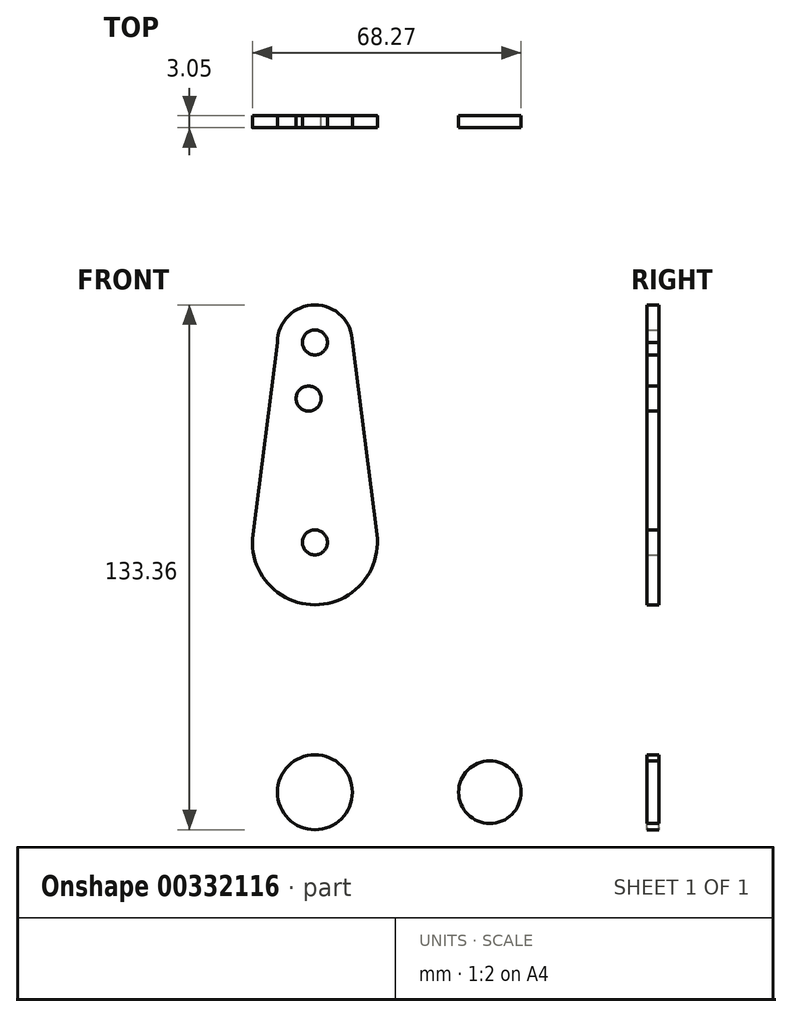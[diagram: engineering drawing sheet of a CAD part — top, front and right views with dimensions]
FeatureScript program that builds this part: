
annotation { "Feature Type Name" : "Feature", "Feature Type Description" : "" }
export const myFeature = defineFeature(function(context is Context, id is Id, definition is map)
    precondition{}
    {
        {
            var Q0;
            Q0=qCreatedBy(makeId("Front.planeOp"),FACE);
            var sketch = newSketch(context, id + "F0", { "sketchPlane" : qUnion([Q0])});
            skLineSegment(sketch, "E0", {"start": v(0, 0) * mm, "end": v(0, 114.3) * mm, "construction": true});
            skLineSegment(sketch, "E1", {"start": v(0, 0) * mm, "end": v(44.45, 0) * mm, "construction": true});
            skCircle(sketch, "E2", {"center": v(0, 114.3) * mm, "radius": 9.53 * mm});
            skCircle(sketch, "E3", {"center": v(0, 63.5) * mm, "radius": 15.88 * mm});
            skCircle(sketch, "E4", {"center": v(0, 0) * mm, "radius": 9.53 * mm});
            skCircle(sketch, "E5", {"center": v(44.45, 0) * mm, "radius": 7.94 * mm});
            skLineSegment(sketch, "E6", {"start": v(-9.53, 114.3) * mm, "end": v(-15.75, 65.5) * mm});
            skLineSegment(sketch, "E7", {"start": v(9.53, 114.3) * mm, "end": v(15.75, 65.5) * mm});
            skLineSegment(sketch, "E8", {"start": v(18.97, 8.85) * mm, "end": v(44.73, 7.93) * mm});
            skLineSegment(sketch, "E9", {"start": v(0, -9.52) * mm, "end": v(44.45, -7.94) * mm});
            skLineSegment(sketch, "E10", {"start": v(15.8, 61.91) * mm, "end": v(11.34, 17.59) * mm});
            skLineSegment(sketch, "E11", {"start": v(-15.8, 61.91) * mm, "end": v(-9.53, 0) * mm});
            skCircle(sketch, "E12", {"center": v(0, 114.3) * mm, "radius": 3.18 * mm});
            skCircle(sketch, "E13", {"center": v(0, 63.5) * mm, "radius": 3.18 * mm});
            skCircle(sketch, "E14", {"center": v(0, 0) * mm, "radius": 3.18 * mm});
            skCircle(sketch, "E15", {"center": v(44.45, 0) * mm, "radius": 3.18 * mm});
            skCircle(sketch, "E16", {"center": v(-1.59, 100.03) * mm, "radius": 3.18 * mm});
            skArc(sketch, "E17.filletArc", {"start": v(11.34, 17.59) * mm, "mid": v(13.26, 11.57) * mm, "end": v(18.97, 8.85) * mm});
            skSolve(sketch);
        }
        {
            var Q0;
            Q0 = qSketchRegion(id + "F0", true);
            extrude(context, id + "F1", {"entities" : qUnion([Q0]), "depth" : 3.05 * mm});
        }
    });
